# Revit family: 69-TAZA CARLTON ADA PARA FLUXOMETRO CASIENTO OPEN RING
name_source: partatom
category: Aparatos sanitarios
units: mm (PartAtom-declared; Revit-internal decimal feet)

## family parameters
Anfitrión = Muro
Compartido = Sí
Corte con vacíos al cargar = Sí
Cota de conector redondo = Diámetro de uso
Número OmniClass = 23.45.00.00
Punto de cálculo de habitación = No
Siempre vertical = Sí
Tipo de pieza = Normal
Título OmniClass = Sanitary, Laundry, and Cleaning Equipment

## types (1)
- TAZA CARLTON ADA PARA FLUXOMETRO C/ASIENTO OPEN RING
    Elevación por defecto = 0 cm
    F_Alto = 47 cm
    F_Ancho = 36 cm
    F_Certificación = Producto certificado por CESMEC en base al cumplimiento de la Norma Chilena NCh 407 2012 para Artefactos Sanitarios de loza vítrea, según modelo de certificación ISO CASCO 5
    F_Color = Blanco
    F_Consumo / Capacidad de agua (L) = 4.8 L
    F_Descripción = Taza de mayor altura para fluxómetro, con descarga de alta eficiencia de 4,8 L, funcionamiento por acción directa con efecto de sifón y sistema jet
    F_Distancia de instalación a muro terminado = 30.5 cm
    F_Peso = 24 kgf
    F_Productos incluidos = Spud y asiento open ring
    F_Productos necesarios para instalación = Fluxómetro, sello de cera y pernos de anclaje
    F_Profundidad = 75.5 cm
    F_SKU = JS9077911300CB
    F_Tipo de aro = Elongado
    F_Tipo de instalación = A piso
    F_Tolerancia dimensional = <20 cm:+- 3%, >20 cm: 0,6 cm máx.
    URL = https://briggs.cl

## geometry (parser evidence)
native form markers: Sweep x3
no freeform markers — native parametric forms only
